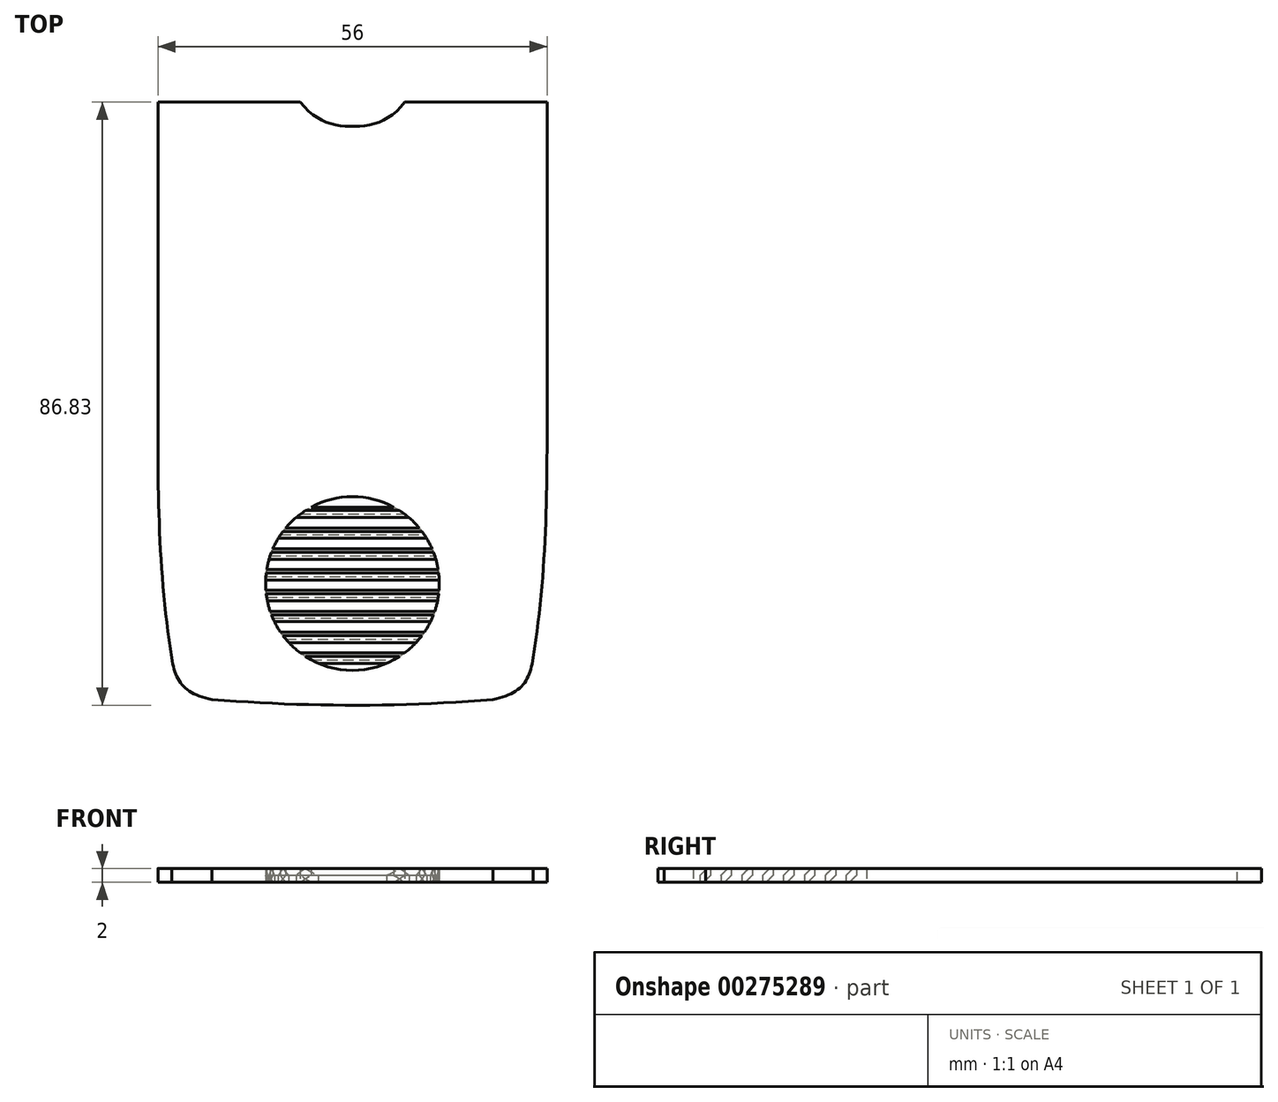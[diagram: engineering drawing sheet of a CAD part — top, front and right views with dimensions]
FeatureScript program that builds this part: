
annotation { "Feature Type Name" : "Feature", "Feature Type Description" : "" }
export const myFeature = defineFeature(function(context is Context, id is Id, definition is map)
    precondition{}
    {
        {
            var Q0;
            Q0=qCreatedBy(makeId("Top.planeOp"),FACE);
            var sketch = newSketch(context, id + "F0", { "sketchPlane" : qUnion([Q0])});
            skLineSegment(sketch, "E0", {"start": v(-28, 80) * mm, "end": v(-7.5, 80) * mm});
            skPoint(sketch, "E1", {"position": v(0, 80) * mm});
            skPoint(sketch, "E2", {"position": v(-7.5, 80) * mm});
            skPoint(sketch, "E3", {"position": v(7.5, 80) * mm});
            skPoint(sketch, "E4", {"position": v(0, 76.5) * mm});
            skFitSpline(sketch, "E5", {"points": [v(-7.5, 80) * mm, v(0, 76.5) * mm, v(7.5, 80) * mm], "startDerivative": vector(13.35, -16.81) * mm, "endDerivative": vector(12.38, 16.81) * mm});
            skLineSegment(sketch, "E6.trimOffspring", {"start": v(7.5, 80) * mm, "end": v(28, 80) * mm});
            skLineSegment(sketch, "E7", {"start": v(-28, 80) * mm, "end": v(-28, 30) * mm});
            skLineSegment(sketch, "E8", {"start": v(28, 80) * mm, "end": v(28, 30) * mm});
            skPoint(sketch, "E9", {"position": v(-26, 0) * mm});
            skLineSegment(sketch, "E10", {"start": v(-28, 30) * mm, "end": v(-28, -24.24) * mm, "construction": true});
            skFitSpline(sketch, "E11", {"points": [v(-28, 30) * mm, v(-26, 0) * mm], "startDerivative": vector(0, -30) * mm, "endDerivative": vector(4.73, -28.9) * mm});
            skPoint(sketch, "E12", {"position": v(-28, 10) * mm});
            skFitSpline(sketch, "E13.MirrorCS", {"points": [v(28, 30) * mm, v(26, 0) * mm], "startDerivative": vector(0, -30) * mm, "endDerivative": vector(-4.73, -28.9) * mm});
            skPoint(sketch, "E14", {"position": v(0, -6.8) * mm});
            skPoint(sketch, "E15", {"position": v(-20, 0) * mm});
            skPoint(sketch, "E16", {"position": v(-20.2, -6) * mm});
            skPoint(sketch, "E17", {"position": v(-24.31, -4.17) * mm});
            skFitSpline(sketch, "E18", {"points": [v(-26, 0) * mm, v(-20.2, -6) * mm], "startDerivative": vector(1.33, -10.1) * mm, "endDerivative": vector(12.02, -2.25) * mm});
            skFitSpline(sketch, "E19.MirrorCS", {"points": [v(26, 0) * mm, v(20.2, -6) * mm], "startDerivative": vector(-1.33, -10.1) * mm, "endDerivative": vector(-12.02, -2.25) * mm});
            skFitSpline(sketch, "E20", {"points": [v(-20.2, -6) * mm, v(20.2, -6) * mm], "startDerivative": vector(39.62, -3.15) * mm, "endDerivative": vector(40.83, 3.52) * mm});
            skLineSegment(sketch, "E21", {"start": v(0, -6.8) * mm, "end": v(0, 28.41) * mm, "construction": true});
            skPoint(sketch, "E22", {"position": v(0, -1.8) * mm});
            skPoint(sketch, "E23", {"position": v(0, 10.7) * mm});
            skCircle(sketch, "E24", {"center": v(0, 10.7) * mm, "radius": 12.5 * mm});
            skPoint(sketch, "E25", {"position": v(0, 23.2) * mm});
            skLineSegment(sketch, "E26.bottom", {"start": v(-5.94, 21.7) * mm, "end": v(5.94, 21.7) * mm});
            skLineSegment(sketch, "E26.top", {"start": v(-8.12, 20.2) * mm, "end": v(8.12, 20.2) * mm});
            skPoint(sketch, "E27", {"position": v(0, 21.7) * mm});
            skLineSegment(sketch, "E28", {"start": v(-9.6, 18.7) * mm, "end": v(9.6, 18.7) * mm});
            skLineSegment(sketch, "E29.1.0.0", {"start": v(-10.68, 17.2) * mm, "end": v(10.68, 17.2) * mm});
            skLineSegment(sketch, "E29.2.0.0", {"start": v(-11.46, 15.7) * mm, "end": v(11.46, 15.7) * mm});
            skLineSegment(sketch, "E29.3.0.0", {"start": v(-12, 14.2) * mm, "end": v(12, 14.2) * mm});
            skLineSegment(sketch, "E29.4.0.0", {"start": v(-12.34, 12.7) * mm, "end": v(12.34, 12.7) * mm});
            skLineSegment(sketch, "E29.5.0.0", {"start": v(-12.49, 11.2) * mm, "end": v(12.49, 11.2) * mm});
            skLineSegment(sketch, "E29.6.0.0", {"start": v(-12.46, 9.7) * mm, "end": v(12.46, 9.7) * mm});
            skLineSegment(sketch, "E29.7.0.0", {"start": v(-12.25, 8.2) * mm, "end": v(12.25, 8.2) * mm});
            skLineSegment(sketch, "E29.8.0.0", {"start": v(-11.84, 6.7) * mm, "end": v(11.84, 6.7) * mm});
            skLineSegment(sketch, "E29.9.0.0", {"start": v(-11.22, 5.2) * mm, "end": v(11.22, 5.2) * mm});
            skLineSegment(sketch, "E29.10.0.0", {"start": v(-10.36, 3.7) * mm, "end": v(10.36, 3.7) * mm});
            skLineSegment(sketch, "E29.11.0.0", {"start": v(-9.17, 2.2) * mm, "end": v(9.17, 2.2) * mm});
            skLineSegment(sketch, "E29.12.0.0", {"start": v(-7.5, 0.7) * mm, "end": v(7.5, 0.7) * mm});
            skLineSegment(sketch, "E29.13.0.0", {"start": v(-4.9, -0.8) * mm, "end": v(4.9, -0.8) * mm});
            skLineSegment(sketch, "E29.direction1", {"start": v(-14.42, 18.7) * mm, "end": v(-14.4, 17.2) * mm, "construction": true});
            skSolve(sketch);
        }
        {
            var Q0;
            Q0=makeQuery(id+"F0.imprint","IMPRINT",FACE,{"disambiguationData":[TD([[makeQuery(id+"F0.imprint","IMPRINT",EDGE,{"derivedFrom":sQuery(id+"F0.wireOp",EDGE,"E0")}),-1.0]])]});
            var Q1;
            {var subQ0=sQuery(id+"F0.wireOp",EDGE,"E26.bottom");Q1=makeQuery(id+"F0.imprint","IMPRINT",FACE,{"disambiguationData":[TD([[makeQuery(id+"F0.imprint","IMPRINT",EDGE,{"derivedFrom":subQ0}),-1.0]])]});}
            var Q2;
            {var subQ0=sQuery(id+"F0.wireOp",EDGE,"E28");Q2=makeQuery(id+"F0.imprint","IMPRINT",FACE,{"disambiguationData":[TD([[makeQuery(id+"F0.imprint","IMPRINT",EDGE,{"derivedFrom":subQ0}),-1.0]])]});}
            var Q3;
            {var subQ0=sQuery(id+"F0.wireOp",EDGE,"E29.2.0.0");Q3=makeQuery(id+"F0.imprint","IMPRINT",FACE,{"disambiguationData":[TD([[makeQuery(id+"F0.imprint","IMPRINT",EDGE,{"derivedFrom":subQ0}),-1.0]])]});}
            var Q4;
            {var subQ0=sQuery(id+"F0.wireOp",EDGE,"E29.4.0.0");Q4=makeQuery(id+"F0.imprint","IMPRINT",FACE,{"disambiguationData":[TD([[makeQuery(id+"F0.imprint","IMPRINT",EDGE,{"derivedFrom":subQ0}),-1.0]])]});}
            var Q5;
            {var subQ0=sQuery(id+"F0.wireOp",EDGE,"E29.6.0.0");Q5=makeQuery(id+"F0.imprint","IMPRINT",FACE,{"disambiguationData":[TD([[makeQuery(id+"F0.imprint","IMPRINT",EDGE,{"derivedFrom":subQ0}),-1.0]])]});}
            var Q6;
            {var subQ0=sQuery(id+"F0.wireOp",EDGE,"E29.8.0.0");Q6=makeQuery(id+"F0.imprint","IMPRINT",FACE,{"disambiguationData":[TD([[makeQuery(id+"F0.imprint","IMPRINT",EDGE,{"derivedFrom":subQ0}),-1.0]])]});}
            var Q7;
            {var subQ0=sQuery(id+"F0.wireOp",EDGE,"E29.10.0.0");Q7=makeQuery(id+"F0.imprint","IMPRINT",FACE,{"disambiguationData":[TD([[makeQuery(id+"F0.imprint","IMPRINT",EDGE,{"derivedFrom":subQ0}),-1.0]])]});}
            var Q8;
            {var subQ0=sQuery(id+"F0.wireOp",EDGE,"E29.12.0.0");Q8=makeQuery(id+"F0.imprint","IMPRINT",FACE,{"disambiguationData":[TD([[makeQuery(id+"F0.imprint","IMPRINT",EDGE,{"derivedFrom":subQ0}),-1.0]])]});}
            extrude(context, id + "F1", {"entities" : qUnion([Q0, Q1, Q2, Q3, Q4, Q5, Q6, Q7, Q8]), "depth" : 2 * mm});
        }
        {
            var Q0;
            Q0=makeQuery(id+"F1.opExtrude","CAP_EDGE",EDGE,{"disambiguationData":[OSD([sQuery(id+"F0.wireOp",EDGE,"E26.bottom")])],"isStart":true});
            var Q1;
            Q1=makeQuery(id+"F1.opExtrude","CAP_EDGE",EDGE,{"disambiguationData":[OSD([sQuery(id+"F0.wireOp",EDGE,"E28")])],"isStart":true});
            var Q2;
            Q2=makeQuery(id+"F1.opExtrude","CAP_EDGE",EDGE,{"disambiguationData":[OSD([sQuery(id+"F0.wireOp",EDGE,"E29.2.0.0")])],"isStart":true});
            var Q3;
            Q3=makeQuery(id+"F1.opExtrude","CAP_EDGE",EDGE,{"disambiguationData":[OSD([sQuery(id+"F0.wireOp",EDGE,"E29.4.0.0")])],"isStart":true});
            var Q4;
            Q4=makeQuery(id+"F1.opExtrude","CAP_EDGE",EDGE,{"disambiguationData":[OSD([sQuery(id+"F0.wireOp",EDGE,"E29.6.0.0")])],"isStart":true});
            var Q5;
            Q5=makeQuery(id+"F1.opExtrude","CAP_EDGE",EDGE,{"disambiguationData":[OSD([sQuery(id+"F0.wireOp",EDGE,"E29.8.0.0")])],"isStart":true});
            var Q6;
            Q6=makeQuery(id+"F1.opExtrude","CAP_EDGE",EDGE,{"disambiguationData":[OSD([sQuery(id+"F0.wireOp",EDGE,"E29.10.0.0")])],"isStart":true});
            var Q7;
            Q7=makeQuery(id+"F1.opExtrude","CAP_EDGE",EDGE,{"disambiguationData":[OSD([sQuery(id+"F0.wireOp",EDGE,"E29.12.0.0")])],"isStart":true});
            var Q8;
            Q8=makeQuery(id+"F1.opExtrude","CAP_EDGE",EDGE,{"disambiguationData":[OSD([sQuery(id+"F0.wireOp",EDGE,"E26.top")])],"isStart":false});
            var Q9;
            Q9=makeQuery(id+"F1.opExtrude","CAP_EDGE",EDGE,{"disambiguationData":[OSD([sQuery(id+"F0.wireOp",EDGE,"E29.1.0.0")])],"isStart":false});
            var Q10;
            Q10=makeQuery(id+"F1.opExtrude","CAP_EDGE",EDGE,{"disambiguationData":[OSD([sQuery(id+"F0.wireOp",EDGE,"E29.3.0.0")])],"isStart":false});
            var Q11;
            Q11=makeQuery(id+"F1.opExtrude","CAP_EDGE",EDGE,{"disambiguationData":[OSD([sQuery(id+"F0.wireOp",EDGE,"E29.5.0.0")])],"isStart":false});
            var Q12;
            Q12=makeQuery(id+"F1.opExtrude","CAP_EDGE",EDGE,{"disambiguationData":[OSD([sQuery(id+"F0.wireOp",EDGE,"E29.7.0.0")])],"isStart":false});
            var Q13;
            Q13=makeQuery(id+"F1.opExtrude","CAP_EDGE",EDGE,{"disambiguationData":[OSD([sQuery(id+"F0.wireOp",EDGE,"E29.9.0.0")])],"isStart":false});
            var Q14;
            Q14=makeQuery(id+"F1.opExtrude","CAP_EDGE",EDGE,{"disambiguationData":[OSD([sQuery(id+"F0.wireOp",EDGE,"E29.13.0.0")])],"isStart":false});
            var Q15;
            Q15=makeQuery(id+"F1.opExtrude","CAP_EDGE",EDGE,{"disambiguationData":[OSD([sQuery(id+"F0.wireOp",EDGE,"E29.11.0.0")])],"isStart":false});
            chamfer(context, id + "F2", {"entities" : qUnion([Q0, Q1, Q2, Q3, Q4, Q5, Q6, Q7, Q8, Q9, Q10, Q11, Q12, Q13, Q14, Q15]), "width" : 1 * mm, "tangentPropagation" : true});
        }
    });
